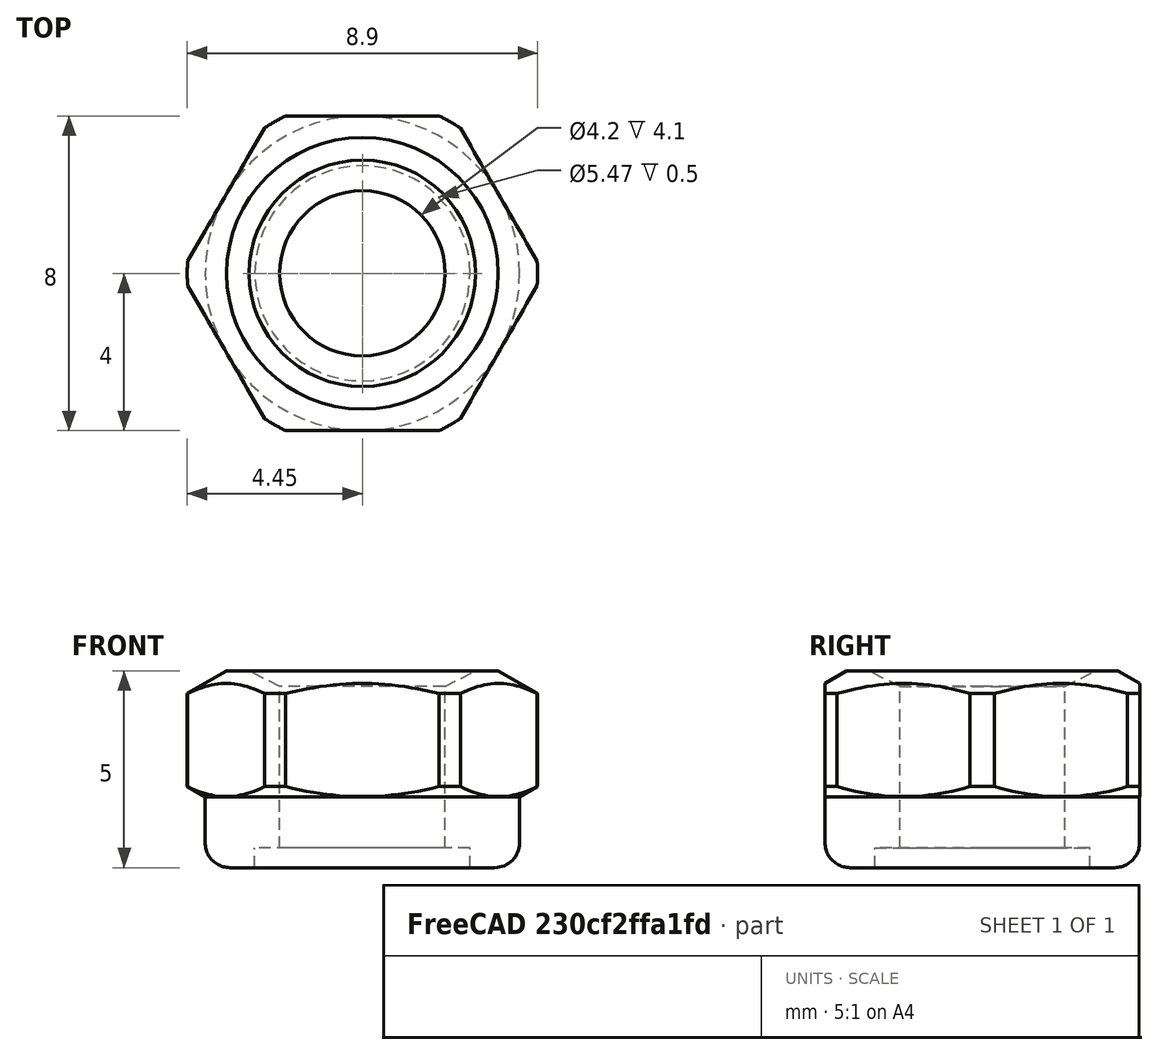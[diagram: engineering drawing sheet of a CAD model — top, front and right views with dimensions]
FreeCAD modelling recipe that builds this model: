
FCSTD DOCUMENT  (FreeCAD 1.0R39319 (Git))
Label: Assy_M5_rod
License: All rights reserved
LicenseURL: https://en.wikipedia.org/wiki/All_rights_reserved
objects: App::DocumentObjectGroup×3, PartDesign::CoordinateSystem×1, App::FeaturePython×1, App::Link×1, Part::FeaturePython×1, App::Part×1
note: 2 computed .brp shape members not serialized (recipe doc carries the construction recipe); baked Part::Feature solids carry a one-line shape summary decoded from their .brp
EXTERNAL_REF file=../../Part/Purchase/M5_rod.FCStd obj=bottom
EXTERNAL_REF file=../../Part/Purchase/M5_rod.FCStd obj=Part

FEATURE [App::DocumentObjectGroup] Parts
FEATURE [PartDesign::CoordinateSystem] LCS_Origin
  AttacherType = Attacher::AttachEngine3D
  AttachmentSupport = -> [X_Axis]
  MapMode = 2
FEATURE [App::DocumentObjectGroup] Constraints
FEATURE [App::FeaturePython] Variables  # WARN: FeaturePython — macro-defined, semantics opaque (R4)
  Type = App::PropertyContainer
FEATURE [App::DocumentObjectGroup] Configurations
FEATURE [App::Link] M5_rod
  AttachedBy = #bottom
  AttachedTo = Parent Assembly#LCS_Origin
  LinkedObject = -> <external ../../Part/Purchase/M5_rod.FCStd>#Part
  SolverId = Asm4EE
  expr: Placement = LCS_Origin.Placement * AttachmentOffset * M5_rod#bottom.Placement ^ -1
FEATURE [Part::FeaturePython] Nut  label="M5-Nut"  # WARN: FeaturePython — macro-defined, semantics opaque (R4)
  Diameter = 3
  Invert = false
  LeftHanded = false
  MatchOuter = false
  Offset = 4
  OffsetAngle = 0
  Placement = pos=(0,6e-16,10) rot=(1,0,0;3.14159rad)
  Thread = false
  Type = 21
FEATURE [App::Part] Assembly  label="Assy_M5_rod"
  AssemblyType = Part::Link
  Group = -> [LCS_Origin,Constraints,Variables,Configurations,M5_rod,Nut]
  Origin = -> Origin
  Type = Assembly

RESOLVED EXTERNAL PARTS (link-assembly join: the EXTERNAL_REF files above that resolve inside this repo's crawl, each included once):
---- part ../../Part/Purchase/M5_rod.FCStd = doc fcstd_2fada063bff4 ----
FCSTD DOCUMENT  (FreeCAD 1.0R39319 (Git))
Label: M5_rod
License: All rights reserved
LicenseURL: https://en.wikipedia.org/wiki/All_rights_reserved
objects: PartDesign::CoordinateSystem×2, Sketcher::SketchObject×1, PartDesign::Pad×1, PartDesign::Chamfer×1, PartDesign::Body×1, App::Part×1
note: 11 computed .brp shape members not serialized (recipe doc carries the construction recipe); baked Part::Feature solids carry a one-line shape summary decoded from their .brp

FEATURE [Sketcher::SketchObject] Sketch
  ArcFitTolerance = 1e-06
  AttachmentSupport = -> [XY_Plane001]
  FullyConstrained = true
  MakeInternals = false
  MapMode = 5
  sketch-geometry (1):
    g0: Circle CenterX=0 CenterY=0 CenterZ=0 NormalX=0 NormalY=0 NormalZ=1 AngleXU=0 Radius=2.5
  constraints (2):
    c: Coincident(g0,g-1)
    c: Diameter(g0) = 5
FEATURE [PartDesign::Pad] Pad
  Direction = (0,0,1)
  Length = 306
  Length2 = 10
  Profile = -> Sketch
  ReferenceAxis = -> Sketch [N_Axis]
  Refine = true
  Suppressed = false
  Type = 0
FEATURE [PartDesign::Chamfer] Chamfer
  Angle = 45
  Base = -> Pad [Edge3,Edge2]
  BaseFeature = -> Pad
  ChamferType = 0
  FlipDirection = false
  Refine = true
  Size = 0.5
  Size2 = 1
  SupportTransform = false
  Suppressed = false
  UseAllEdges = false
FEATURE [PartDesign::Body] Body  label="M5_rod001"
  AllowCompound = false
  Group = -> [Sketch,Pad,Chamfer]
  Origin = -> Origin001
  Tip = -> Chamfer
FEATURE [PartDesign::CoordinateSystem] bottom
  AttacherType = Attacher::AttachEngine3D
  AttachmentSupport = -> [Chamfer]
FEATURE [PartDesign::CoordinateSystem] nut
  AttacherType = Attacher::AttachEngine3D
  AttachmentOffset = pos=(0,0,5) rot=(0,0,1;0rad)
  AttachmentSupport = -> [Chamfer]
  MapMode = 11
  Placement = pos=(0,0,5) rot=(0,0,1;1.5708rad)
FEATURE [App::Part] Part  label="M5_rod"
  Group = -> [Body,bottom,nut]
  Origin = -> Origin
